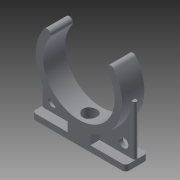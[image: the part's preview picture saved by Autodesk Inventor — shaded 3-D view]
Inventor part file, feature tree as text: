
AUTODESK INVENTOR PART (.ipt)
format: ipt  version: 2019 (Build 230136000, 136)  size: 168,448 bytes
history: native  units: in
note: dims shown in document units (in); Inventor stores cm internally (conversion verified against a paired STEP export)
features: fillet x1, other x1, imported_body x1
ambient origin geometry x8: Origin, YZ Plane, XZ Plane, XY Plane, X Axis, Y Axis, Z Axis, Center Point
bodies: Body1 (feature_tree)
feature tree (3):
  fillet  "Fillet3"  [1 undecoded]
  other  "am-20081"
  imported_body  "Base1"
note: 1 required parameter value undecoded (feature->parameter linkage not recoverable at this tier; creation-order binding heuristic only, values carry confidence <= 0.55)
